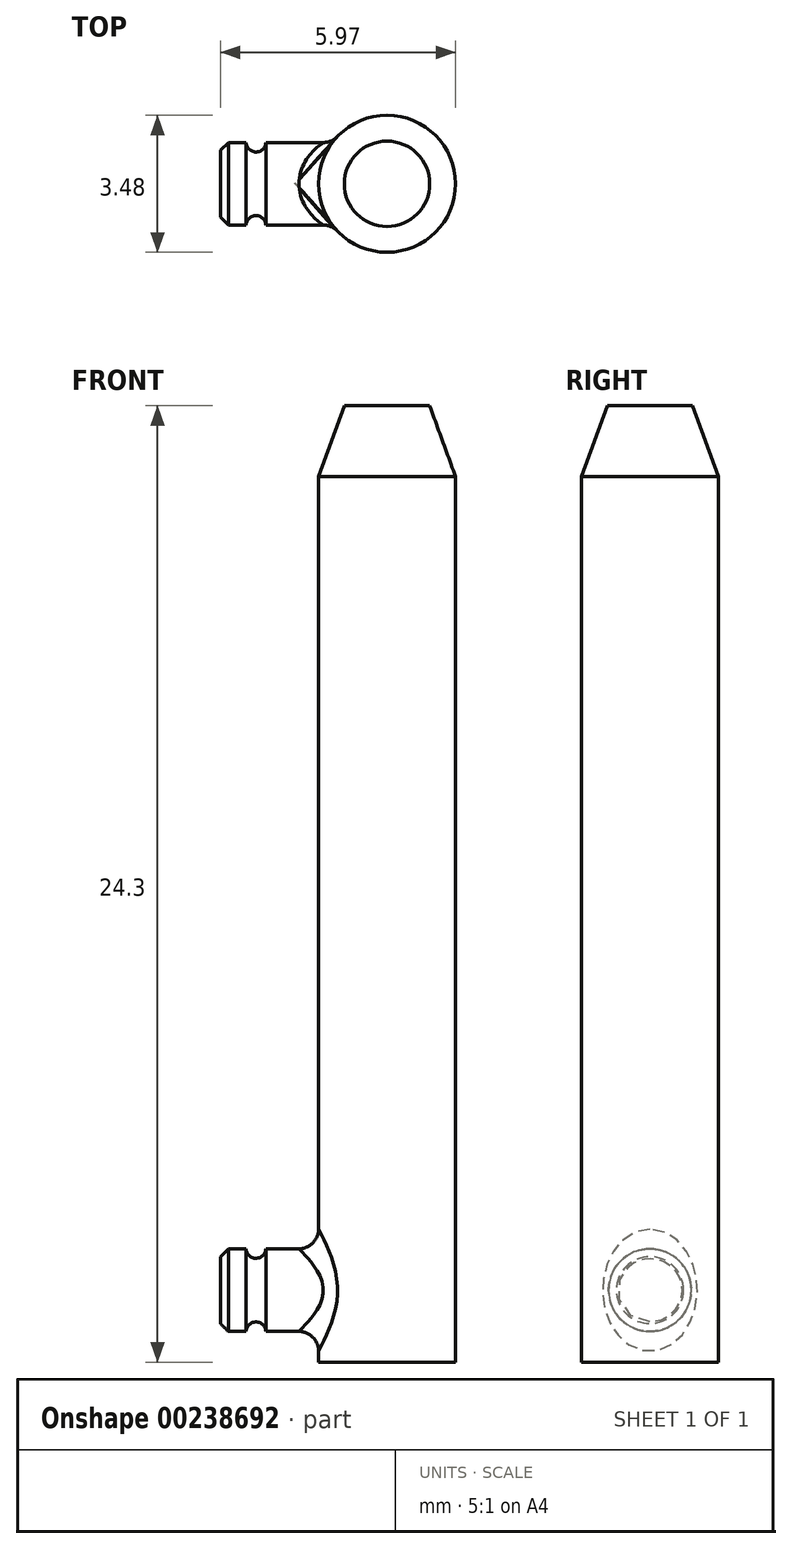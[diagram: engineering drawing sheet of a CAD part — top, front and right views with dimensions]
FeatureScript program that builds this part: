
annotation { "Feature Type Name" : "Feature", "Feature Type Description" : "" }
export const myFeature = defineFeature(function(context is Context, id is Id, definition is map)
    precondition{}
    {
        {
            var Q0;
            Q0=qCreatedBy(makeId("Top.planeOp"),FACE);
            var sketch = newSketch(context, id + "F0", { "sketchPlane" : qUnion([Q0])});
            skCircle(sketch, "E0", {"center": v(0, 0) * mm, "radius": 1.74 * mm});
            skSolve(sketch);
        }
        {
            var Q0;
            Q0=makeQuery(id+"F0.imprint","IMPRINT",FACE,{"disambiguationData":[TD([[makeQuery(id+"F0.imprint","IMPRINT",EDGE,{"derivedFrom":sQuery(id+"F0.wireOp",EDGE,"E0")}),1.0]])]});
            extrude(context, id + "F1", {"entities" : qUnion([Q0]), "depth" : 24.3 * mm});
        }
        {
            var Q0;
            Q0=makeQuery(id+"F1.opExtrude","CAP_EDGE",EDGE,{"disambiguationData":[OSD([sQuery(id+"F0.wireOp",EDGE,"E0")])],"isStart":false});
            chamfer(context, id + "F2", {"entities" : qUnion([Q0]), "chamferType" : ChamferType.OFFSET_ANGLE, "width" : 1.8 * mm, "oppositeDirection" : true, "angle" : 20 * degree});
        }
        {
            var Q0;
            Q0=qCreatedBy(makeId("Right.planeOp"),FACE);
            var sketch = newSketch(context, id + "F3", { "sketchPlane" : qUnion([Q0])});
            skCircle(sketch, "E1", {"center": v(0, 1.83) * mm, "radius": 1.05 * mm});
            skSolve(sketch);
        }
        {
            var Q0;
            Q0=makeQuery(id+"F3.imprint","IMPRINT",FACE,{"disambiguationData":[TD([[makeQuery(id+"F3.imprint","IMPRINT",EDGE,{"derivedFrom":sQuery(id+"F3.wireOp",EDGE,"E1")}),1.0]])]});
            extrude(context, id + "F4", {"entities" : qUnion([Q0]), "operationType" : NewBodyOperationType.ADD, "oppositeDirection" : true, "depth" : 4.23 * mm});
        }
        {
            var Q0;
            Q0=qCreatedBy(makeId("Front.planeOp"),FACE);
            var sketch = newSketch(context, id + "F5", { "sketchPlane" : qUnion([Q0])});
            skLineSegment(sketch, "E2", {"start": v(-3.58, 4.6) * mm, "end": v(-3.58, 2.9) * mm});
            skLineSegment(sketch, "E3", {"start": v(-3.08, 4.6) * mm, "end": v(-3.08, 2.9) * mm});
            skLineSegment(sketch, "E4", {"start": v(-3.58, 4.6) * mm, "end": v(-3.08, 4.6) * mm});
            skArc(sketch, "E5", {"start": v(-3.58, 2.9) * mm, "mid": v(-3.33, 2.64) * mm, "end": v(-3.08, 2.9) * mm});
            skSolve(sketch);
        }
        {
            var Q0;
            Q0=makeQuery(id+"F5.imprint","IMPRINT",FACE,{"disambiguationData":[TD([[makeQuery(id+"F5.imprint","IMPRINT",EDGE,{"derivedFrom":sQuery(id+"F5.wireOp",EDGE,"E2")}),1.0]])]});
            var Q1;
            Q1=makeQuery(id+"F4.opExtrude","CAP_EDGE",EDGE,{"disambiguationData":[OSD([sQuery(id+"F3.wireOp",EDGE,"E1")])],"isStart":false});
            revolve(context, id + "F6", {"operationType" : NewBodyOperationType.REMOVE, "entities" : qUnion([Q0]), "axis" : qUnion([Q1]), "revolveType" : RevolveType.FULL, "oppositeDirection" : true});
        }
        {
            var Q0;
            Q0=makeQuery(id+"F4.opExtrude","CAP_EDGE",EDGE,{"disambiguationData":[OSD([sQuery(id+"F3.wireOp",EDGE,"E1")])],"isStart":false});
            chamfer(context, id + "F7", {"entities" : qUnion([Q0]), "width" : 0.2 * mm, "tangentPropagation" : true});
        }
        {
            var Q0;
            Q0=makeQuery(id+"F4.boolean.opBoolean","INTERSECT",EDGE,{"derivedFrom":[makeQuery(id+"F1.opExtrude","SWEPT_FACE",FACE,{"disambiguationData":[OSD([sQuery(id+"F0.wireOp",EDGE,"E0")])]}),makeQuery(id+"F4.opExtrude","SWEPT_FACE",FACE,{"disambiguationData":[OSD([sQuery(id+"F3.wireOp",EDGE,"E1")])]})]});
            fillet(context, id + "F8", {"entities" : qUnion([Q0]), "radius" : .5 * mm, "tangentPropagation" : true, "allowEdgeOverflow" : false});
        }
    });
